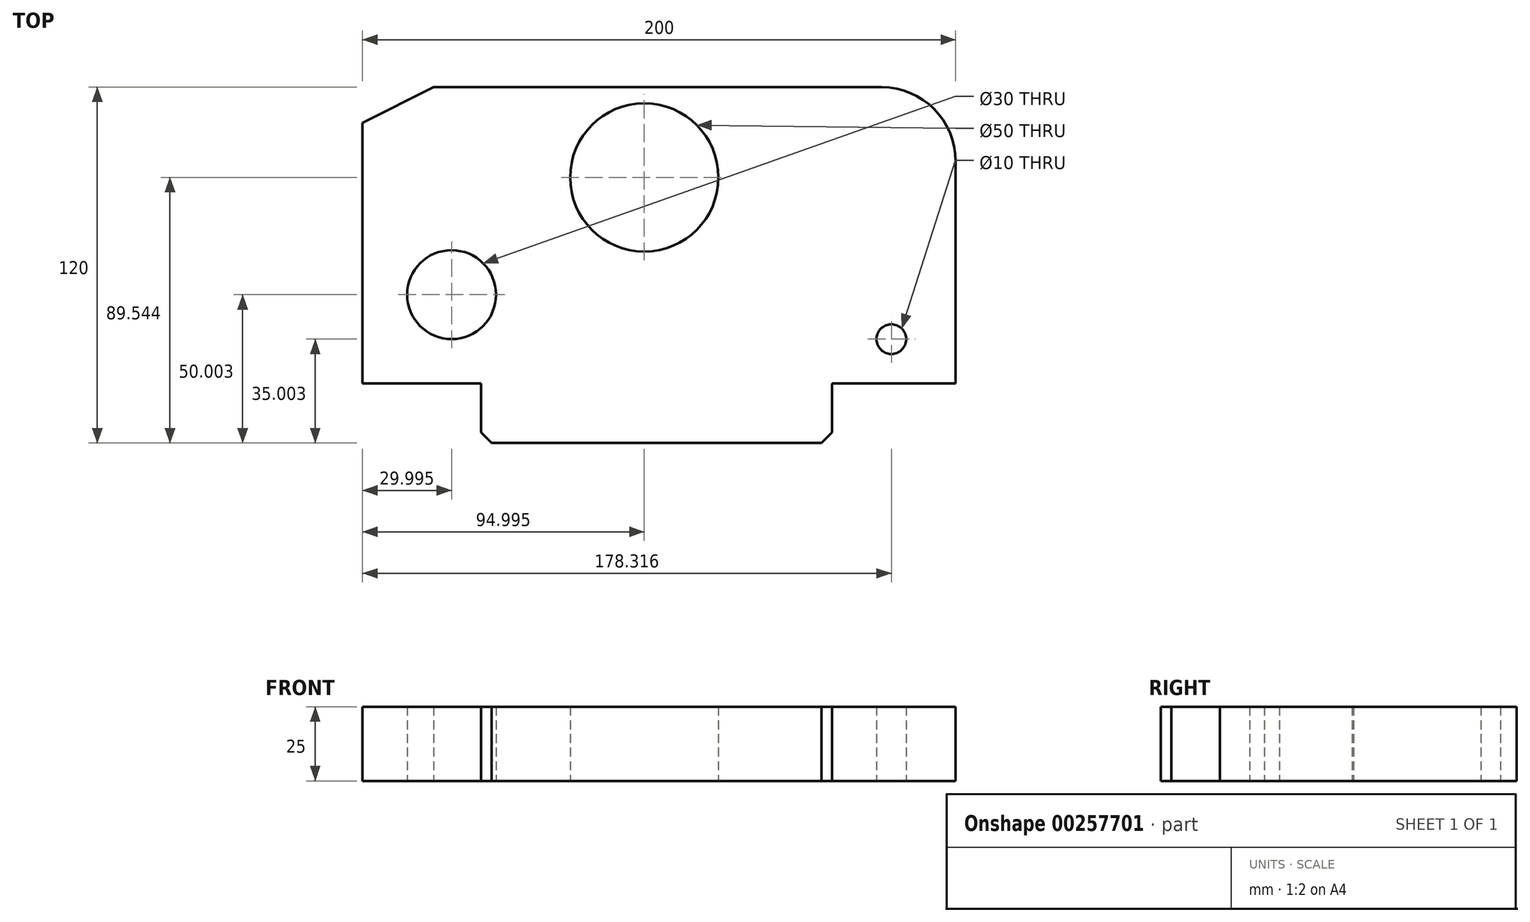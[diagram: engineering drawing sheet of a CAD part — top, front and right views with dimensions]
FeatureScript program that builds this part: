
annotation { "Feature Type Name" : "Feature", "Feature Type Description" : "" }
export const myFeature = defineFeature(function(context is Context, id is Id, definition is map)
    precondition{}
    {
        {
            var Q0;
            Q0=qCreatedBy(makeId("Top.planeOp"),FACE);
            var sketch = newSketch(context, id + "F0", { "sketchPlane" : qUnion([Q0])});
            skLineSegment(sketch, "E0", {"start": v(-63.5, -37.12) * mm, "end": v(-63.5, -20.66) * mm});
            skLineSegment(sketch, "E1", {"start": v(-63.5, -20.66) * mm, "end": v(-73.5, -20.66) * mm});
            skLineSegment(sketch, "E2", {"start": v(-73.5, -20.66) * mm, "end": v(-103.5, -20.66) * mm});
            skLineSegment(sketch, "E3", {"start": v(-103.5, -20.66) * mm, "end": v(-103.5, 9.34) * mm});
            skLineSegment(sketch, "E4", {"start": v(-103.5, 9.34) * mm, "end": v(-103.5, 67.34) * mm});
            skLineSegment(sketch, "E5", {"start": v(-103.5, 67.34) * mm, "end": v(-79.5, 79.34) * mm});
            skLineSegment(sketch, "E6", {"start": v(-79.5, 79.34) * mm, "end": v(-8.5, 79.34) * mm});
            skLineSegment(sketch, "E7", {"start": v(-8.5, 79.34) * mm, "end": v(71.5, 79.34) * mm});
            skLineSegment(sketch, "E8", {"start": v(96.5, 54.34) * mm, "end": v(96.5, -5.66) * mm});
            skLineSegment(sketch, "E9", {"start": v(96.5, -5.66) * mm, "end": v(96.5, -20.66) * mm});
            skLineSegment(sketch, "E10", {"start": v(-59.96, -40.66) * mm, "end": v(51.3, -40.66) * mm});
            skPoint(sketch, "E11.end.orphan", {"position": v(74.83, -20.66) * mm});
            skLineSegment(sketch, "E12", {"start": v(54.83, -37.12) * mm, "end": v(54.83, -20.66) * mm});
            skPoint(sketch, "E13", {"position": v(-73.5, 9.34) * mm});
            skLineSegment(sketch, "E14", {"start": v(96.5, -20.66) * mm, "end": v(74.83, -20.66) * mm});
            skLineSegment(sketch, "E15", {"start": v(54.83, -20.66) * mm, "end": v(74.83, -20.66) * mm});
            skPoint(sketch, "E16", {"position": v(74.83, -5.66) * mm});
            skPoint(sketch, "E17.visualSharp", {"position": v(96.5, 79.34) * mm});
            skArc(sketch, "E17.filletArc", {"start": v(96.5, 54.34) * mm, "mid": v(89.18, 72.02) * mm, "end": v(71.5, 79.34) * mm});
            skPoint(sketch, "E18", {"position": v(-8.5, 48.88) * mm});
            skCircle(sketch, "E19", {"center": v(-8.5, 48.88) * mm, "radius": 25 * mm});
            skCircle(sketch, "E20", {"center": v(-73.5, 9.34) * mm, "radius": 15 * mm});
            skCircle(sketch, "E21", {"center": v(74.83, -5.66) * mm, "radius": 5 * mm});
            skLineSegment(sketch, "E22", {"start": v(-63.5, -37.12) * mm, "end": v(-59.96, -40.66) * mm});
            skPoint(sketch, "E23", {"position": v(54.83, -37.12) * mm});
            skLineSegment(sketch, "E24", {"start": v(54.83, -37.12) * mm, "end": v(51.3, -40.66) * mm});
            skSolve(sketch);
        }
        {
            var Q0;
            Q0=makeQuery(id+"F0.imprint","IMPRINT",FACE,{"disambiguationData":[TD([[makeQuery(id+"F0.imprint","IMPRINT",EDGE,{"derivedFrom":sQuery(id+"F0.wireOp",EDGE,"E0")}),-1.0]])]});
            extrude(context, id + "F1", {"entities" : qUnion([Q0]), "depth" : 25 * mm});
        }
    });
